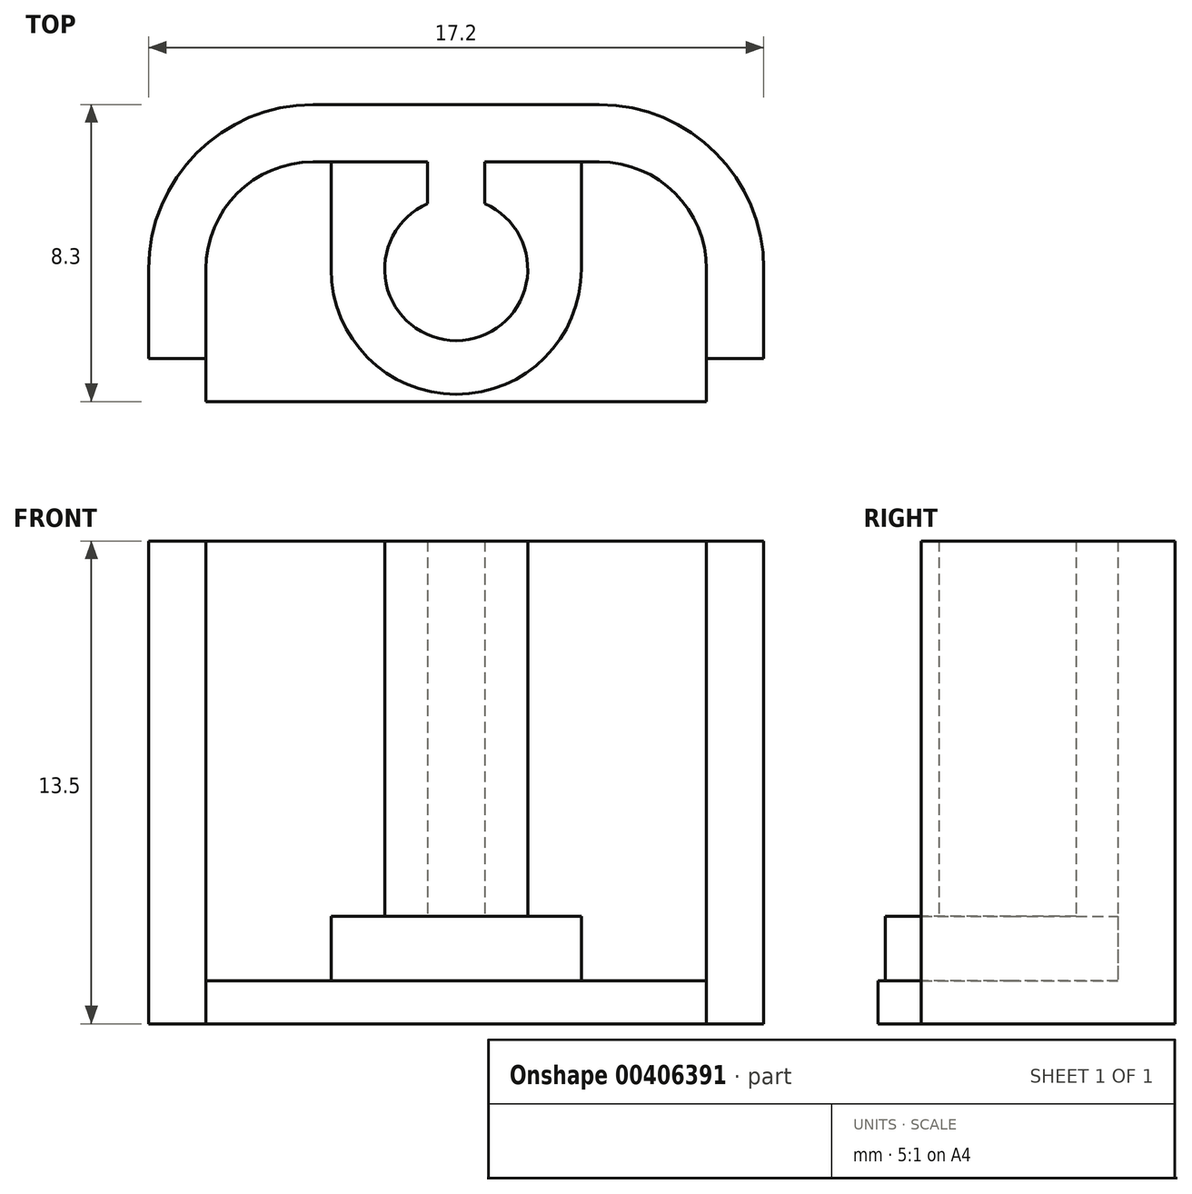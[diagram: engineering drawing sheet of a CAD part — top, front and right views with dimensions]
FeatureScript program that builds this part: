
annotation { "Feature Type Name" : "Feature", "Feature Type Description" : "" }
export const myFeature = defineFeature(function(context is Context, id is Id, definition is map)
    precondition{}
    {
        {
            var Q0;
            Q0=qCreatedBy(makeId("Top.planeOp"),FACE);
            var sketch = newSketch(context, id + "F0", { "sketchPlane" : qUnion([Q0])});
            skLineSegment(sketch, "E0.bottom", {"start": v(-8.6, -2.5) * mm, "end": v(-7, -2.5) * mm});
            skLineSegment(sketch, "E0.top", {"start": v(-4, 4.6) * mm, "end": v(4, 4.6) * mm});
            skLineSegment(sketch, "E0.left", {"start": v(-8.6, -2.5) * mm, "end": v(-8.6, 0) * mm});
            skLineSegment(sketch, "E0.right", {"start": v(8.6, -2.5) * mm, "end": v(8.6, 0) * mm});
            skArc(sketch, "E1", {"start": v(-0.8, 1.83) * mm, "mid": v(0, -2) * mm, "end": v(0.8, 1.83) * mm});
            skLineSegment(sketch, "E2", {"start": v(-0.8, 1.83) * mm, "end": v(-0.8, 3) * mm});
            skLineSegment(sketch, "E3", {"start": v(-0.8, 3) * mm, "end": v(-4, 3) * mm});
            skLineSegment(sketch, "E4", {"start": v(-7, 0) * mm, "end": v(-7, -2.5) * mm});
            skLineSegment(sketch, "E5", {"start": v(0.8, 1.83) * mm, "end": v(0.8, 3) * mm});
            skLineSegment(sketch, "E6", {"start": v(0.8, 3) * mm, "end": v(4, 3) * mm});
            skLineSegment(sketch, "E7", {"start": v(7, 0) * mm, "end": v(7, -2.5) * mm});
            skLineSegment(sketch, "E8.trimOffspring", {"start": v(7, -2.5) * mm, "end": v(8.6, -2.5) * mm});
            skLineSegment(sketch, "E9", {"start": v(-0.8, 3) * mm, "end": v(0.8, 3) * mm, "construction": true});
            skLineSegment(sketch, "E10", {"start": v(0, 3) * mm, "end": v(0, 0) * mm, "construction": true});
            skPoint(sketch, "E11.visualSharp", {"position": v(-7, 3) * mm});
            skArc(sketch, "E11.filletArc", {"start": v(-4, 3) * mm, "mid": v(-6.12, 2.12) * mm, "end": v(-7, 0) * mm});
            skPoint(sketch, "E12.visualSharp", {"position": v(7, 3) * mm});
            skArc(sketch, "E12.filletArc", {"start": v(7, 0) * mm, "mid": v(6.12, 2.12) * mm, "end": v(4, 3) * mm});
            skArc(sketch, "E13", {"start": v(-4, 4.6) * mm, "mid": v(-7.25, 3.25) * mm, "end": v(-8.6, 0) * mm});
            skArc(sketch, "E14", {"start": v(8.6, 0) * mm, "mid": v(7.25, 3.25) * mm, "end": v(4, 4.6) * mm});
            skSolve(sketch);
        }
        {
            var Q0;
            Q0 = qSketchRegion(id + "F0", true);
            extrude(context, id + "F1", {"entities" : qUnion([Q0]), "depth" : 13.5 * mm, "offsetDistance" : 25 * mm});
        }
        {
            var Q0;
            Q0=makeQuery(id+"F1.opExtrude","CAP_FACE",FACE,{"disambiguationData":[OSD([sQuery(id+"F0.wireOp",EDGE,"E0.bottom"),sQuery(id+"F0.wireOp",EDGE,"E0.top"),sQuery(id+"F0.wireOp",EDGE,"E0.left"),sQuery(id+"F0.wireOp",EDGE,"E0.right"),sQuery(id+"F0.wireOp",EDGE,"E1"),sQuery(id+"F0.wireOp",EDGE,"E2"),sQuery(id+"F0.wireOp",EDGE,"E3"),sQuery(id+"F0.wireOp",EDGE,"E4"),sQuery(id+"F0.wireOp",EDGE,"E5"),sQuery(id+"F0.wireOp",EDGE,"E6"),sQuery(id+"F0.wireOp",EDGE,"E7"),sQuery(id+"F0.wireOp",EDGE,"E8.trimOffspring"),sQuery(id+"F0.wireOp",EDGE,"E11.filletArc"),sQuery(id+"F0.wireOp",EDGE,"E12.filletArc"),sQuery(id+"F0.wireOp",EDGE,"E13"),sQuery(id+"F0.wireOp",EDGE,"E14")])],"isStart":true});
            var sketch = newSketch(context, id + "F2", { "sketchPlane" : qUnion([Q0])});
            skLineSegment(sketch, "E15.0", {"start": v(-8.6, 2.5) * mm, "end": v(-8.6, 0) * mm});
            skArc(sketch, "E15.1", {"start": v(-4, -4.6) * mm, "mid": v(-7.25, -3.25) * mm, "end": v(-8.6, 0) * mm});
            skLineSegment(sketch, "E15.2", {"start": v(-4, -4.6) * mm, "end": v(4, -4.6) * mm});
            skArc(sketch, "E15.3", {"start": v(8.6, 0) * mm, "mid": v(7.25, -3.25) * mm, "end": v(4, -4.6) * mm});
            skLineSegment(sketch, "E15.4", {"start": v(8.6, 2.5) * mm, "end": v(8.6, 0) * mm});
            skLineSegment(sketch, "E16", {"start": v(-8.6, 2.5) * mm, "end": v(-7, 2.5) * mm});
            skLineSegment(sketch, "E17", {"start": v(-7, 2.5) * mm, "end": v(-7, 3.7) * mm});
            skLineSegment(sketch, "E18", {"start": v(-7, 3.7) * mm, "end": v(7, 3.7) * mm});
            skLineSegment(sketch, "E19", {"start": v(7, 3.7) * mm, "end": v(7, 2.5) * mm});
            skLineSegment(sketch, "E20.trimOffspring", {"start": v(7, 2.5) * mm, "end": v(8.6, 2.5) * mm});
            skSolve(sketch);
        }
        {
            var Q0;
            Q0 = qSketchRegion(id + "F2", true);
            extrude(context, id + "F3", {"entities" : qUnion([Q0]), "operationType" : NewBodyOperationType.ADD, "oppositeDirection" : true, "depth" : 1.2 * mm, "offsetDistance" : 25 * mm});
        }
        {
            var Q0;
            Q0=makeQuery(id+"F3.opExtrude","CAP_FACE",FACE,{"disambiguationData":[OSD([sQuery(id+"F2.wireOp",EDGE,"E15.0"),sQuery(id+"F2.wireOp",EDGE,"E15.1"),sQuery(id+"F2.wireOp",EDGE,"E15.2"),sQuery(id+"F2.wireOp",EDGE,"E15.3"),sQuery(id+"F2.wireOp",EDGE,"E15.4"),sQuery(id+"F2.wireOp",EDGE,"E16"),sQuery(id+"F2.wireOp",EDGE,"E17"),sQuery(id+"F2.wireOp",EDGE,"E18"),sQuery(id+"F2.wireOp",EDGE,"E19"),sQuery(id+"F2.wireOp",EDGE,"E20.trimOffspring")])],"isStart":false});
            var sketch = newSketch(context, id + "F4", { "sketchPlane" : qUnion([Q0])});
            skArc(sketch, "E21", {"start": v(-3.5, 0) * mm, "mid": v(0, -3.5) * mm, "end": v(3.5, 0) * mm});
            skLineSegment(sketch, "E22", {"start": v(-3.5, 0) * mm, "end": v(-3.5, 3) * mm});
            skLineSegment(sketch, "E23", {"start": v(-3.5, 3) * mm, "end": v(3.5, 3) * mm});
            skLineSegment(sketch, "E24", {"start": v(3.5, 3) * mm, "end": v(3.5, 0) * mm});
            skSolve(sketch);
        }
        {
            var Q0;
            Q0 = qSketchRegion(id + "F4", true);
            extrude(context, id + "F5", {"entities" : qUnion([Q0]), "operationType" : NewBodyOperationType.ADD, "depth" : 1.8 * mm, "offsetDistance" : 25 * mm});
        }
    });
